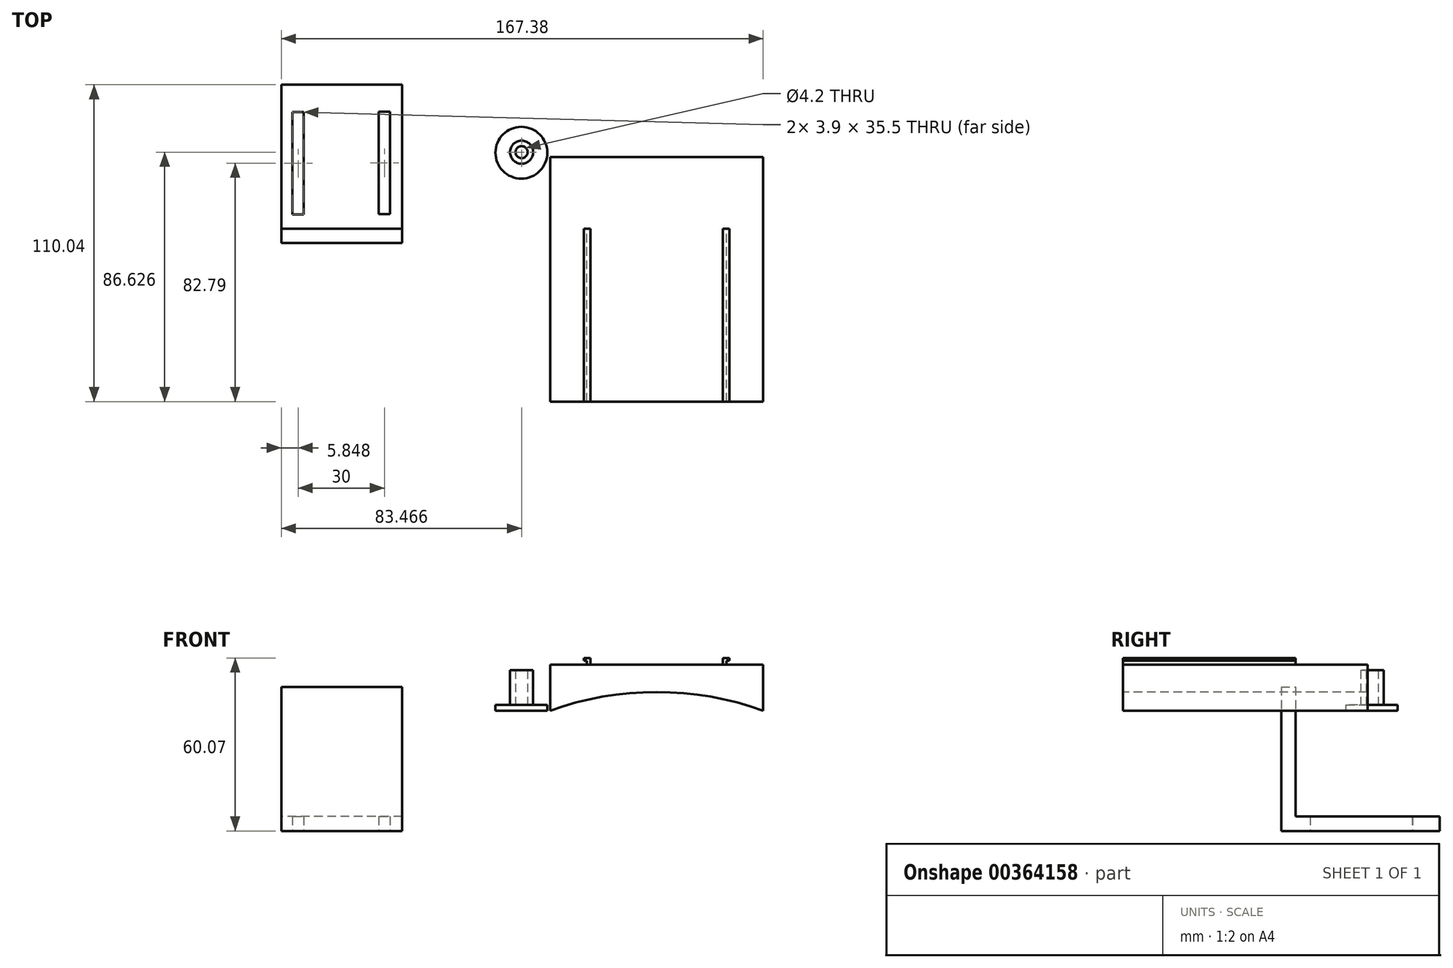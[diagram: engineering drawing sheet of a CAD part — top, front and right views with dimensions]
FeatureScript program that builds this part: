
annotation { "Feature Type Name" : "Feature", "Feature Type Description" : "" }
export const myFeature = defineFeature(function(context is Context, id is Id, definition is map)
    precondition{}
    {
        {
            var Q0;
            Q0=qCreatedBy(makeId("Top.planeOp"),FACE);
            var sketch = newSketch(context, id + "F0", { "sketchPlane" : qUnion([Q0])});
            skCircle(sketch, "E0", {"center": v(-32.52, 26.4) * mm, "radius": 9 * mm});
            skSolve(sketch);
        }
        {
            var Q0;
            Q0=qCreatedBy(makeId("Top.planeOp"),FACE);
            var sketch = newSketch(context, id + "F1", { "sketchPlane" : qUnion([Q0])});
            skCircle(sketch, "E1", {"center": v(-32.45, 26.59) * mm, "radius": 4 * mm});
            skCircle(sketch, "E2", {"center": v(-32.45, 26.59) * mm, "radius": 2.1 * mm});
            skSolve(sketch);
        }
        {
            var Q0;
            Q0 = qSketchRegion(id + "F0", true);
            extrude(context, id + "F2", {"entities" : qUnion([Q0]), "depth" : 2 * mm});
        }
        {
            var Q0;
            Q0 = qSketchRegion(id + "F1", true);
            extrude(context, id + "F3", {"entities" : qUnion([Q0]), "operationType" : NewBodyOperationType.ADD, "depth" : 14 * mm});
        }
        {
            var Q0;
            Q0=makeQuery(id+"F3.boolean.opBoolean","SPLIT",FACE,{"disambiguationData":[TD([makeQuery(id+"F3.opExtrude","SWEPT_FACE",FACE,{"disambiguationData":[OSD([sQuery(id+"F1.wireOp",EDGE,"E2")])]})])],"derivedFrom":makeQuery(id+"F2.opExtrude","CAP_FACE",FACE,{"disambiguationData":[OSD([sQuery(id+"F0.wireOp",EDGE,"E0")])],"isStart":false})});
            extrude(context, id + "F4", {"entities" : qUnion([Q0]), "operationType" : NewBodyOperationType.REMOVE, "oppositeDirection" : true, "depth" : 2 * mm});
        }
        {
            var Q0;
            Q0=qCreatedBy(makeId("Top.planeOp"),FACE);
            var sketch = newSketch(context, id + "F5", { "sketchPlane" : qUnion([Q0])});
            skLineSegment(sketch, "E3.bottom", {"start": v(-22.54, 24.96) * mm, "end": v(51.46, 24.96) * mm});
            skLineSegment(sketch, "E3.top", {"start": v(-22.54, -60.04) * mm, "end": v(51.46, -60.04) * mm});
            skLineSegment(sketch, "E3.left", {"start": v(-22.54, 24.96) * mm, "end": v(-22.54, -60.04) * mm});
            skLineSegment(sketch, "E3.right", {"start": v(51.46, 24.96) * mm, "end": v(51.46, -60.04) * mm});
            skSolve(sketch);
        }
        {
            var Q0;
            Q0=makeQuery(id+"F5.imprint","IMPRINT",FACE,{"disambiguationData":[TD([[makeQuery(id+"F5.imprint","IMPRINT",EDGE,{"derivedFrom":sQuery(id+"F5.wireOp",EDGE,"E3.bottom")}),-1.0]])]});
            extrude(context, id + "F6", {"entities" : qUnion([Q0]), "depth" : 16 * mm});
        }
        {
            var Q0;
            Q0=makeQuery(id+"F6.opExtrude","SWEPT_FACE",FACE,{"disambiguationData":[OSD([sQuery(id+"F5.wireOp",EDGE,"E3.top")])]});
            var sketch = newSketch(context, id + "F7", { "sketchPlane" : qUnion([Q0])});
            skCircle(sketch, "E4", {"center": v(14.46, -102.53) * mm, "radius": 109 * mm});
            skPoint(sketch, "E4.first.point", {"position": v(-22.54, 0) * mm});
            skPoint(sketch, "E4.second.point", {"position": v(51.46, 0) * mm});
            skPoint(sketch, "E4.third.point", {"position": v(108.65, -157.4) * mm});
            skSolve(sketch);
        }
        {
            var Q0;
            {var subQ1=sQuery(id+"F5.wireOp",EDGE,"E3.top");var subQ2=makeQuery(id+"F6.opExtrude","CAP_EDGE",EDGE,{"disambiguationData":[OSD([subQ1])],"isStart":true});Q0=makeQuery(id+"F7.imprint","IMPRINT",FACE,{"disambiguationData":[TD([[makeQuery(id+"F7.imprint","IMPRINT",EDGE,{"derivedFrom":subQ2}),1.0]])]});}
            extrude(context, id + "F8", {"entities" : qUnion([Q0]), "operationType" : NewBodyOperationType.REMOVE, "oppositeDirection" : true, "depth" : 85 * mm});
        }
        {
            var Q0;
            Q0=qCreatedBy(makeId("Front.planeOp"),FACE);
            var sketch = newSketch(context, id + "F9", { "sketchPlane" : qUnion([Q0])});
            skLineSegment(sketch, "E5", {"start": v(-8.54, 16) * mm, "end": v(-8.54, 18.3) * mm});
            skLineSegment(sketch, "E6", {"start": v(-10.84, 18.3) * mm, "end": v(-8.54, 18.3) * mm});
            skLineSegment(sketch, "E7", {"start": v(-10.84, 18.3) * mm, "end": v(-10.84, 17.3) * mm});
            skLineSegment(sketch, "E8", {"start": v(-10.84, 17.3) * mm, "end": v(-9.84, 17.3) * mm});
            skLineSegment(sketch, "E9", {"start": v(-9.84, 17.3) * mm, "end": v(-9.84, 16) * mm});
            skLineSegment(sketch, "E10", {"start": v(-9.84, 16) * mm, "end": v(-8.54, 16) * mm});
            skLineSegment(sketch, "E11", {"start": v(37.46, 16) * mm, "end": v(37.46, 18.3) * mm});
            skLineSegment(sketch, "E12", {"start": v(37.46, 18.3) * mm, "end": v(39.76, 18.3) * mm});
            skLineSegment(sketch, "E13", {"start": v(39.76, 17.3) * mm, "end": v(39.76, 18.3) * mm});
            skLineSegment(sketch, "E14", {"start": v(39.76, 17.3) * mm, "end": v(38.76, 17.3) * mm});
            skLineSegment(sketch, "E15", {"start": v(38.76, 17.3) * mm, "end": v(38.76, 16) * mm});
            skLineSegment(sketch, "E16", {"start": v(38.76, 16) * mm, "end": v(37.46, 16) * mm});
            skSolve(sketch);
        }
        {
            var Q0;
            Q0=makeQuery(id+"F9.imprint","IMPRINT",FACE,{"disambiguationData":[TD([[makeQuery(id+"F9.imprint","IMPRINT",EDGE,{"derivedFrom":sQuery(id+"F9.wireOp",EDGE,"E5")}),1.0]])]});
            var Q1;
            Q1=makeQuery(id+"F9.imprint","IMPRINT",FACE,{"disambiguationData":[TD([[makeQuery(id+"F9.imprint","IMPRINT",EDGE,{"derivedFrom":sQuery(id+"F9.wireOp",EDGE,"E11")}),-1.0]])]});
            extrude(context, id + "F10", {"entities" : qUnion([Q0, Q1]), "depth" : 60 * mm});
        }
        {
            var Q0;
            Q0=qCreatedBy(makeId("Front.planeOp"),FACE);
            var sketch = newSketch(context, id + "F11", { "sketchPlane" : qUnion([Q0])});
            skLineSegment(sketch, "E17.bottom", {"start": v(-115.92, 8.23) * mm, "end": v(-73.92, 8.23) * mm});
            skLineSegment(sketch, "E17.top", {"start": v(-115.92, -41.77) * mm, "end": v(-73.92, -41.77) * mm});
            skLineSegment(sketch, "E17.left", {"start": v(-115.92, 8.23) * mm, "end": v(-115.92, -41.77) * mm});
            skLineSegment(sketch, "E17.right", {"start": v(-73.92, 8.23) * mm, "end": v(-73.92, -41.77) * mm});
            skSolve(sketch);
        }
        {
            var Q0;
            Q0 = qSketchRegion(id + "F11", true);
            extrude(context, id + "F12", {"entities" : qUnion([Q0]), "depth" : 5 * mm});
        }
        {
            var Q0;
            Q0=makeQuery(id+"F12.opExtrude","CAP_FACE",FACE,{"disambiguationData":[OSD([sQuery(id+"F11.wireOp",EDGE,"E17.bottom"),sQuery(id+"F11.wireOp",EDGE,"E17.top"),sQuery(id+"F11.wireOp",EDGE,"E17.left"),sQuery(id+"F11.wireOp",EDGE,"E17.right")])],"isStart":true});
            var sketch = newSketch(context, id + "F13", { "sketchPlane" : qUnion([Q0])});
            skLineSegment(sketch, "E18.bottom", {"start": v(73.92, -41.77) * mm, "end": v(115.92, -41.77) * mm});
            skLineSegment(sketch, "E18.top", {"start": v(73.92, -36.77) * mm, "end": v(115.92, -36.77) * mm});
            skLineSegment(sketch, "E18.left", {"start": v(73.92, -41.77) * mm, "end": v(73.92, -36.77) * mm});
            skLineSegment(sketch, "E18.right", {"start": v(115.92, -41.77) * mm, "end": v(115.92, -36.77) * mm});
            skSolve(sketch);
        }
        {
            var Q0;
            Q0 = qSketchRegion(id + "F13", true);
            extrude(context, id + "F14", {"entities" : qUnion([Q0]), "operationType" : NewBodyOperationType.ADD, "depth" : 50 * mm});
        }
        {
            var Q0;
            Q0=makeQuery(id+"F14.boolean.opBoolean","MERGE",FACE,{"derivedFrom":[makeQuery(id+"F12.opExtrude","SWEPT_FACE",FACE,{"disambiguationData":[OSD([sQuery(id+"F11.wireOp",EDGE,"E17.top")])]}),makeQuery(id+"F14.opExtrude","SWEPT_FACE",FACE,{"disambiguationData":[OSD([sQuery(id+"F13.wireOp",EDGE,"E18.bottom")])]})]});
            var sketch = newSketch(context, id + "F15", { "sketchPlane" : qUnion([Q0])});
            skLineSegment(sketch, "E19.bottom", {"start": v(-112.02, -5) * mm, "end": v(-108.12, -5) * mm});
            skLineSegment(sketch, "E19.top", {"start": v(-112.02, -40.5) * mm, "end": v(-108.12, -40.5) * mm});
            skLineSegment(sketch, "E19.left", {"start": v(-112.02, -5) * mm, "end": v(-112.02, -40.5) * mm});
            skLineSegment(sketch, "E19.right", {"start": v(-108.12, -5) * mm, "end": v(-108.12, -40.5) * mm});
            skLineSegment(sketch, "E20.1.0.0", {"start": v(-82.02, -5.1) * mm, "end": v(-78.12, -5.1) * mm});
            skLineSegment(sketch, "E20.1.0.1", {"start": v(-82.02, -40.6) * mm, "end": v(-78.12, -40.6) * mm});
            skLineSegment(sketch, "E20.1.0.2", {"start": v(-82.02, -5.1) * mm, "end": v(-82.02, -40.6) * mm});
            skLineSegment(sketch, "E20.1.0.3", {"start": v(-78.12, -5.1) * mm, "end": v(-78.12, -40.6) * mm});
            skLineSegment(sketch, "E20.direction1", {"start": v(-108.12, -40.5) * mm, "end": v(-78.12, -40.6) * mm, "construction": true});
            skSolve(sketch);
        }
        {
            var Q0;
            Q0 = qSketchRegion(id + "F15", true);
            extrude(context, id + "F16", {"entities" : qUnion([Q0]), "operationType" : NewBodyOperationType.REMOVE, "oppositeDirection" : true, "depth" : 5 * mm});
        }
    });
